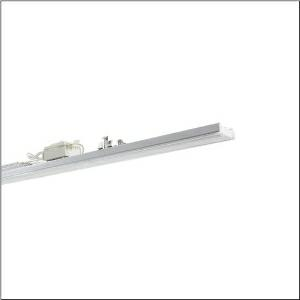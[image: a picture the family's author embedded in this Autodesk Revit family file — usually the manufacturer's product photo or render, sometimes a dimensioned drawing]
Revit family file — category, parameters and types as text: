
# Revit family: licross_21_recessed_ho_52tl1edv4l2s
name_source: partatom
category: Lighting Fixtures
units: mm (PartAtom-declared; Revit-internal decimal feet)

## family parameters
Cut with Voids When Loaded = No
Host = Face
Light Source = No
Part Type = Normal
Room Calculation Point = No
Round Connector Dimension = Use Diameter
Shared = No

## types (1)
- --- (1 x LED, 22130 lm, 125.6 W, 4000K)
    Apparent Load = 126 VA
    CIE Flux Codes = 85 95 99 100 100
    Color Rendering = 80
    Color Temperature = 4000K
    Default Elevation = 1800 mm
    Description = Licross 21 Recessed HO, luminaire insert, of sheet steel, galvanised, coil coated, white, length: 2.250mm, width: 66mm, height: 67mm, LED rated luminous flux: 22.130lm, light colour: 840, SDCM (Standard Deviation of Colour Matching)MacAdam ≤ 3 SDCM (initial), control gear: DALI 2, with plug, 5-pole, with phase selection, mains connection: 220..240V, AC, 50/60Hz, rated input power: 126W, internal wiring halogen-free, primary light control with lens, of plastic, primary optical cover: cover, of PMMA, light emission: direct distribution, primary light characteristic: symmetric, protection rating (complete): IP40, insulation class (complete): insulation class I (protective earthing), certification: CE, ENEC, VDE, UKCA, protection symbol: D if used in an environment without relevant dust loads with corresponding accessories, impact resistance: IK06, permissible ambient temperature for indoor applications: -40..+30°C, corresponds to IFS (International Featured Standards) requirements for safety and quality in the food industry, reducing of maximum allowable ambient temperature of 5°C with ceiling mounting, LABS conformity tested according to VDMA 24364:2018-05, The light source and the operating device comply with the requirements of the Ecodesign Regulation (EU) 2019/2020 and are replaceable in accordance with this regulation, packaging unit: 1 piece
    Height = 58 mm
    Lamp = 1 x LED
    Lamp Light Flux = 22130 lm
    Lamp Power = 125.6 W
    Lamp count = 1
    Length = 2250 mm
    Luminous efficacy = 176 lm/W
    Manufacturer = Siteco
    ModVariant = No
    Model = 52TL1EDV4L2S
    Mounting Place = Ceiling
    Mounting Type = Pendant
    Number of Poles = 1
    OnlyDefault = Yes
    Power Factor = 1
    Product Name = Licross 21 Recessed HO
    Product group = luminaire insert | ceiling pendant
    ProductGroupID = 901
    Protection Class = Protection class I
    Protection Degree = IP 40
    RLX_Detail_Level = 1
    RLX_Emergency_Light_Flux = 0 lm
    RLX_Emergency_Type = 0
    RLX_Emergency_Type_DB = No
    RlxData = <blob elided: 29997 chars, md5=dc426440>
    Socket = socket
    Standby Power = 0 W
    System Light Flux = 22129 lm
    System Power = 126 W
    Type Comments = factory setting: luminous flux: 100 % | dim-lin: 254 | 489 mA
    Type Image = l_1296930.jpg
    URL = http://relux.com
    VarID = @adj_125715
    Voltage = 0 V
    Weight = 0.00 kg
    Width = 66 mm

## geometry (parser evidence)
native form markers: Blend x4, Sweep x9
no freeform markers — native parametric forms only
